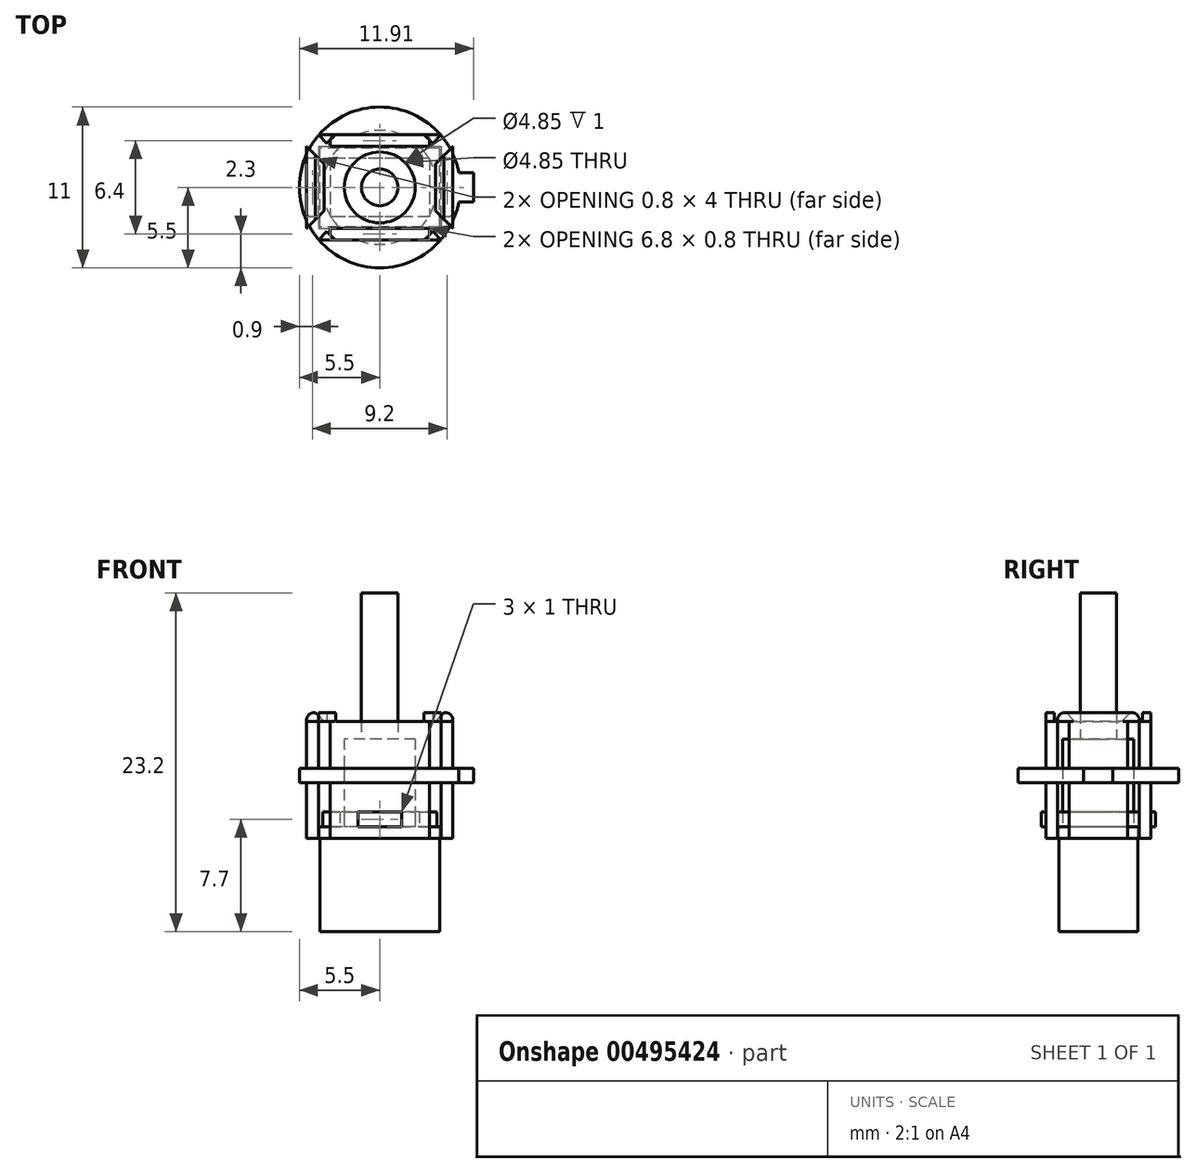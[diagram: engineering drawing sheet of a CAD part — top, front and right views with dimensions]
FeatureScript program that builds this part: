
annotation { "Feature Type Name" : "Feature", "Feature Type Description" : "" }
export const myFeature = defineFeature(function(context is Context, id is Id, definition is map)
    precondition{}
    {
        {
            assignVariable(context, id + "F0", {"name" : "wall", "anyValue" : 0.8});
        }
        {
            assignVariable(context, id + "F1", {"name" : "switch_height", "anyValue" : 7.2});
        }
        {
            var Q0;
            Q0=qCreatedBy(makeId("Top.planeOp"),FACE);
            var sketch = newSketch(context, id + "F2", { "sketchPlane" : qUnion([Q0])});
            skLineSegment(sketch, "E0.bottom", {"start": v(4.1, -2.7) * mm, "end": v(-4.1, -2.7) * mm});
            skLineSegment(sketch, "E0.top", {"start": v(4.1, 2.7) * mm, "end": v(-4.1, 2.7) * mm});
            skLineSegment(sketch, "E0.left", {"start": v(4.1, -2.7) * mm, "end": v(4.1, 2.7) * mm});
            skLineSegment(sketch, "E0.right", {"start": v(-4.1, -2.7) * mm, "end": v(-4.1, 2.7) * mm});
            skPoint(sketch, "E0.middle", {"position": v(0, 0) * mm});
            skCircle(sketch, "E1", {"center": v(0, 0) * mm, "radius": 2.43 * mm});
            skCircle(sketch, "E2", {"center": v(0, 0) * mm, "radius": 3.9 * mm});
            skCircle(sketch, "E3", {"center": v(0, 0) * mm, "radius": 5.5 * mm});
            skLineSegment(sketch, "E4.bottom", {"start": v(5.4, -1) * mm, "end": v(6.4, -1) * mm});
            skLineSegment(sketch, "E4.top", {"start": v(5.4, 1) * mm, "end": v(6.4, 1) * mm});
            skLineSegment(sketch, "E4.left", {"start": v(5.4, -1) * mm, "end": v(5.4, 1) * mm});
            skLineSegment(sketch, "E4.right", {"start": v(6.4, -1) * mm, "end": v(6.4, 1) * mm});
            skPoint(sketch, "E4.middle", {"position": v(5.9, 0) * mm});
            skPoint(sketch, "E4.middle.positionSnap0", {"position": v(4.1, 0) * mm});
            skPoint(sketch, "E4.centerSnap0", {"position": v(4.1, 0) * mm});
            skCircle(sketch, "E5", {"center": v(0, 0) * mm, "radius": 1.25 * mm});
            skSolve(sketch);
        }
        {
            var Q0;
            Q0=makeQuery(id+"F2.imprint","IMPRINT",FACE,{"disambiguationData":[TD([[makeQuery(id+"F2.imprint","IMPRINT",EDGE,{"derivedFrom":sQuery(id+"F2.wireOp",EDGE,"E0.bottom")}),-1.0]])]});
            var Q1;
            Q1=makeQuery(id+"F2.imprint","IMPRINT",FACE,{"disambiguationData":[TD([[makeQuery(id+"F2.imprint","IMPRINT",EDGE,{"derivedFrom":sQuery(id+"F2.wireOp",EDGE,"E1")}),1.0]])]});
            var Q2;
            Q2=makeQuery(id+"F2.imprint","IMPRINT",FACE,{"disambiguationData":[TD([[makeQuery(id+"F2.imprint","IMPRINT",EDGE,{"derivedFrom":sQuery(id+"F2.wireOp",EDGE,"E1")}),-1.0]])]});
            var Q3;
            Q3=makeQuery(id+"F2.imprint","IMPRINT",FACE,{"disambiguationData":[TD([[makeQuery(id+"F2.imprint","IMPRINT",EDGE,{"derivedFrom":sQuery(id+"F2.wireOp",EDGE,"E5")}),1.0]])]});
            extrude(context, id + "F3", {"entities" : qUnion([Q0, Q1, Q2, Q3]), "oppositeDirection" : true, "depth" : (getVariable(context, 'switch_height')) * mm});
        }
        {
            var Q0;
            Q0=makeQuery(id+"F2.imprint","IMPRINT",FACE,{"disambiguationData":[TD([[makeQuery(id+"F2.imprint","IMPRINT",EDGE,{"derivedFrom":sQuery(id+"F2.wireOp",EDGE,"E1")}),1.0]])]});
            var Q1;
            Q1=makeQuery(id+"F2.imprint","IMPRINT",FACE,{"disambiguationData":[TD([[makeQuery(id+"F2.imprint","IMPRINT",EDGE,{"derivedFrom":sQuery(id+"F2.wireOp",EDGE,"E5")}),1.0]])]});
            extrude(context, id + "F4", {"entities" : qUnion([Q0, Q1]), "operationType" : NewBodyOperationType.ADD, "depth" : 6 * mm});
        }
        {
            var Q0;
            Q0=makeQuery(id+"F2.imprint","IMPRINT",FACE,{"disambiguationData":[TD([[makeQuery(id+"F2.imprint","IMPRINT",EDGE,{"derivedFrom":sQuery(id+"F2.wireOp",EDGE,"E1")}),-1.0]])]});
            var Q1;
            {var subQ0=sQuery(id+"F2.wireOp",EDGE,"E2");var subQ1=sQuery(id+"F2.wireOp",EDGE,"E0.bottom");var subQ2=makeQuery(id+"F2.imprint","INTERSECT",VERTEX,{"disambiguationData":[OD(0.0)],"derivedFrom":[subQ1,subQ0]});Q1=makeQuery(id+"F2.imprint","IMPRINT",FACE,{"disambiguationData":[TD([[makeQuery(id+"F2.imprint","IMPRINT",EDGE,{"disambiguationData":[TD([[subQ2,-1.0]])],"derivedFrom":subQ1}),1.0]])]});}
            var Q2;
            {var subQ0=sQuery(id+"F2.wireOp",EDGE,"E2");var subQ1=sQuery(id+"F2.wireOp",EDGE,"E0.top");var subQ2=makeQuery(id+"F2.imprint","INTERSECT",VERTEX,{"disambiguationData":[OD(0.0)],"derivedFrom":[subQ1,subQ0]});Q2=makeQuery(id+"F2.imprint","IMPRINT",FACE,{"disambiguationData":[TD([[makeQuery(id+"F2.imprint","IMPRINT",EDGE,{"disambiguationData":[TD([[subQ2,-1.0]])],"derivedFrom":subQ1}),-1.0]])]});}
            extrude(context, id + "F5", {"entities" : qUnion([Q0, Q1, Q2]), "depth" : 1 * mm});
        }
        {
            var Q0;
            {var subQ0=sQuery(id+"F2.wireOp",EDGE,"E0.left");Q0=makeQuery(id+"F2.imprint","IMPRINT",FACE,{"disambiguationData":[TD([[makeQuery(id+"F2.imprint","IMPRINT",EDGE,{"derivedFrom":subQ0}),-1.0]])]});}
            var Q1;
            {var subQ0=sQuery(id+"F2.wireOp",EDGE,"E0.right");Q1=makeQuery(id+"F2.imprint","IMPRINT",FACE,{"disambiguationData":[TD([[makeQuery(id+"F2.imprint","IMPRINT",EDGE,{"derivedFrom":subQ0}),-1.0]])]});}
            var Q2;
            {var subQ0=sQuery(id+"F2.wireOp",EDGE,"E0.left");Q2=makeQuery(id+"F2.imprint","IMPRINT",FACE,{"disambiguationData":[TD([[makeQuery(id+"F2.imprint","IMPRINT",EDGE,{"derivedFrom":subQ0}),1.0]])]});}
            var Q3;
            {var subQ1=sQuery(id+"F2.wireOp",EDGE,"E4.bottom");Q3=makeQuery(id+"F2.imprint","IMPRINT",FACE,{"disambiguationData":[TD([[makeQuery(id+"F2.imprint","IMPRINT",EDGE,{"derivedFrom":subQ1}),1.0]])]});}
            var Q4;
            {var subQ0=sQuery(id+"F2.wireOp",EDGE,"E4.left");Q4=makeQuery(id+"F2.imprint","IMPRINT",FACE,{"disambiguationData":[TD([[makeQuery(id+"F2.imprint","IMPRINT",EDGE,{"derivedFrom":subQ0}),-1.0]])]});}
            var Q5;
            {var subQ0=sQuery(id+"F2.wireOp",EDGE,"E2");var subQ1=sQuery(id+"F2.wireOp",EDGE,"E0.top");var subQ2=makeQuery(id+"F2.imprint","INTERSECT",VERTEX,{"disambiguationData":[OD(0.0)],"derivedFrom":[subQ1,subQ0]});Q5=makeQuery(id+"F2.imprint","IMPRINT",FACE,{"disambiguationData":[TD([[makeQuery(id+"F2.imprint","IMPRINT",EDGE,{"disambiguationData":[TD([[subQ2,-1.0]])],"derivedFrom":subQ1}),-1.0]])]});}
            var Q6;
            Q6=makeQuery(id+"F2.imprint","IMPRINT",FACE,{"disambiguationData":[TD([[makeQuery(id+"F2.imprint","IMPRINT",EDGE,{"derivedFrom":sQuery(id+"F2.wireOp",EDGE,"E1")}),-1.0]])]});
            var Q7;
            {var subQ0=sQuery(id+"F2.wireOp",EDGE,"E2");var subQ1=sQuery(id+"F2.wireOp",EDGE,"E0.bottom");var subQ2=makeQuery(id+"F2.imprint","INTERSECT",VERTEX,{"disambiguationData":[OD(0.0)],"derivedFrom":[subQ1,subQ0]});Q7=makeQuery(id+"F2.imprint","IMPRINT",FACE,{"disambiguationData":[TD([[makeQuery(id+"F2.imprint","IMPRINT",EDGE,{"disambiguationData":[TD([[subQ2,-1.0]])],"derivedFrom":subQ1}),1.0]])]});}
            extrude(context, id + "F6", {"entities" : qUnion([Q0, Q1, Q2, Q3, Q4, Q5, Q6, Q7]), "depth" : 4 * mm, "hasSecondDirection" : true, "secondDirectionOppositeDirection" : true, "secondDirectionDepth" : -3 * mm});
        }
        {
            var Q0;
            Q0=makeQuery(id+"F2.imprint","IMPRINT",FACE,{"disambiguationData":[TD([[makeQuery(id+"F2.imprint","IMPRINT",EDGE,{"derivedFrom":sQuery(id+"F2.wireOp",EDGE,"E5")}),1.0]])]});
            extrude(context, id + "F7", {"entities" : qUnion([Q0]), "operationType" : NewBodyOperationType.ADD, "depth" : 16 * mm});
        }
        {
            var Q0;
            Q0=qCreatedBy(makeId("Top.planeOp"),FACE);
            var sketch = newSketch(context, id + "F8", { "sketchPlane" : qUnion([Q0])});
            skPoint(sketch, "E6.0", {"position": v(0, 0) * mm});
            skLineSegment(sketch, "E7.0", {"start": v(4.1, -2.7) * mm, "end": v(-4.1, -2.7) * mm, "construction": true});
            skLineSegment(sketch, "E8.0", {"start": v(-4.1, -2.7) * mm, "end": v(-4.1, 2.7) * mm, "construction": true});
            skLineSegment(sketch, "E9.0", {"start": v(4.1, 2.7) * mm, "end": v(-4.1, 2.7) * mm, "construction": true});
            skLineSegment(sketch, "E10.0", {"start": v(4.1, -2.7) * mm, "end": v(4.1, 2.7) * mm, "construction": true});
            skLineSegment(sketch, "E11.bottom", {"start": v(5, 2) * mm, "end": v(-5, 2) * mm});
            skLineSegment(sketch, "E11.top", {"start": v(5, -2) * mm, "end": v(-5, -2) * mm});
            skLineSegment(sketch, "E11.left", {"start": v(5, 2) * mm, "end": v(5, -2) * mm});
            skLineSegment(sketch, "E11.right", {"start": v(-5, 2) * mm, "end": v(-5, -2) * mm});
            skLineSegment(sketch, "E12.bottom", {"start": v(3.4, 3.6) * mm, "end": v(-3.4, 3.6) * mm});
            skLineSegment(sketch, "E12.top", {"start": v(3.4, -3.6) * mm, "end": v(-3.4, -3.6) * mm});
            skLineSegment(sketch, "E12.left", {"start": v(3.4, 3.6) * mm, "end": v(3.4, -3.6) * mm});
            skLineSegment(sketch, "E12.right", {"start": v(-3.4, 3.6) * mm, "end": v(-3.4, -3.6) * mm});
            skLineSegment(sketch, "E13.bottom", {"start": v(-4.2, 2.8) * mm, "end": v(4.2, 2.8) * mm});
            skLineSegment(sketch, "E13.top", {"start": v(-4.2, -2.8) * mm, "end": v(4.2, -2.8) * mm});
            skLineSegment(sketch, "E13.left", {"start": v(-4.2, 2.8) * mm, "end": v(-4.2, -2.8) * mm});
            skLineSegment(sketch, "E13.right", {"start": v(4.2, 2.8) * mm, "end": v(4.2, -2.8) * mm});
            skSolve(sketch);
        }
        {
            var Q0;
            {var subQ0=sQuery(id+"F8.wireOp",EDGE,"E12.left");var subQ1=sQuery(id+"F8.wireOp",EDGE,"E9.0");var subQ2=makeQuery(id+"F8.imprint","INTERSECT",VERTEX,{"derivedFrom":[subQ1,subQ0]});Q0=makeQuery(id+"F8.imprint","IMPRINT",FACE,{"disambiguationData":[TD([[makeQuery(id+"F8.imprint","IMPRINT",EDGE,{"disambiguationData":[TD([[subQ2,-1.0]])],"derivedFrom":subQ1}),1.0]])]});}
            var Q1;
            {var subQ0=sQuery(id+"F8.wireOp",EDGE,"E9.0");var subQ1=sQuery(id+"F8.wireOp",EDGE,"E8.0");var subQ2=makeQuery(id+"F8.imprint","INTERSECT",VERTEX,{"derivedFrom":[subQ1,subQ0]});Q1=makeQuery(id+"F8.imprint","IMPRINT",FACE,{"disambiguationData":[TD([[makeQuery(id+"F8.imprint","IMPRINT",EDGE,{"disambiguationData":[TD([[subQ2,1.0]])],"derivedFrom":subQ1}),-1.0]])]});}
            var Q2;
            {var subQ0=sQuery(id+"F8.wireOp",EDGE,"E11.top");var subQ1=sQuery(id+"F8.wireOp",EDGE,"E8.0");var subQ2=makeQuery(id+"F8.imprint","INTERSECT",VERTEX,{"derivedFrom":[subQ1,subQ0]});Q2=makeQuery(id+"F8.imprint","IMPRINT",FACE,{"disambiguationData":[TD([[makeQuery(id+"F8.imprint","IMPRINT",EDGE,{"disambiguationData":[TD([[subQ2,-1.0]])],"derivedFrom":subQ1}),-1.0]])]});}
            var Q3;
            {var subQ0=sQuery(id+"F8.wireOp",EDGE,"E8.0");var subQ1=sQuery(id+"F8.wireOp",EDGE,"E7.0");var subQ2=makeQuery(id+"F8.imprint","INTERSECT",VERTEX,{"derivedFrom":[subQ1,subQ0]});Q3=makeQuery(id+"F8.imprint","IMPRINT",FACE,{"disambiguationData":[TD([[makeQuery(id+"F8.imprint","IMPRINT",EDGE,{"disambiguationData":[TD([[subQ2,1.0]])],"derivedFrom":subQ1}),-1.0]])]});}
            var Q4;
            {var subQ0=sQuery(id+"F8.wireOp",EDGE,"E12.left");var subQ1=sQuery(id+"F8.wireOp",EDGE,"E7.0");var subQ2=makeQuery(id+"F8.imprint","INTERSECT",VERTEX,{"derivedFrom":[subQ1,subQ0]});Q4=makeQuery(id+"F8.imprint","IMPRINT",FACE,{"disambiguationData":[TD([[makeQuery(id+"F8.imprint","IMPRINT",EDGE,{"disambiguationData":[TD([[subQ2,-1.0]])],"derivedFrom":subQ1}),-1.0]])]});}
            var Q5;
            {var subQ0=sQuery(id+"F8.wireOp",EDGE,"E11.top");var subQ1=sQuery(id+"F8.wireOp",EDGE,"E10.0");var subQ2=makeQuery(id+"F8.imprint","INTERSECT",VERTEX,{"derivedFrom":[subQ1,subQ0]});Q5=makeQuery(id+"F8.imprint","IMPRINT",FACE,{"disambiguationData":[TD([[makeQuery(id+"F8.imprint","IMPRINT",EDGE,{"disambiguationData":[TD([[subQ2,-1.0]])],"derivedFrom":subQ1}),1.0]])]});}
            var Q6;
            {var subQ0=sQuery(id+"F8.wireOp",EDGE,"E10.0");var subQ1=sQuery(id+"F8.wireOp",EDGE,"E7.0");var subQ2=makeQuery(id+"F8.imprint","INTERSECT",VERTEX,{"derivedFrom":[subQ1,subQ0]});Q6=makeQuery(id+"F8.imprint","IMPRINT",FACE,{"disambiguationData":[TD([[makeQuery(id+"F8.imprint","IMPRINT",EDGE,{"disambiguationData":[TD([[subQ2,-1.0]])],"derivedFrom":subQ1}),-1.0]])]});}
            var Q7;
            {var subQ0=sQuery(id+"F8.wireOp",EDGE,"E10.0");var subQ1=sQuery(id+"F8.wireOp",EDGE,"E9.0");var subQ2=makeQuery(id+"F8.imprint","INTERSECT",VERTEX,{"derivedFrom":[subQ1,subQ0]});Q7=makeQuery(id+"F8.imprint","IMPRINT",FACE,{"disambiguationData":[TD([[makeQuery(id+"F8.imprint","IMPRINT",EDGE,{"disambiguationData":[TD([[subQ2,-1.0]])],"derivedFrom":subQ1}),1.0]])]});}
            var Q8;
            {var subQ0=sQuery(id+"F8.wireOp",EDGE,"E11.right");Q8=makeQuery(id+"F8.imprint","IMPRINT",FACE,{"disambiguationData":[TD([[makeQuery(id+"F8.imprint","IMPRINT",EDGE,{"derivedFrom":subQ0}),1.0]])]});}
            var Q9;
            {var subQ0=sQuery(id+"F8.wireOp",EDGE,"E13.left");var subQ1=sQuery(id+"F8.wireOp",EDGE,"E11.bottom");var subQ2=makeQuery(id+"F8.imprint","INTERSECT",VERTEX,{"derivedFrom":[subQ1,subQ0]});Q9=makeQuery(id+"F8.imprint","IMPRINT",FACE,{"disambiguationData":[TD([[makeQuery(id+"F8.imprint","IMPRINT",EDGE,{"disambiguationData":[TD([[subQ2,1.0]])],"derivedFrom":subQ1}),1.0]])]});}
            var Q10;
            {var subQ0=sQuery(id+"F8.wireOp",EDGE,"E12.left");var subQ1=sQuery(id+"F8.wireOp",EDGE,"E11.bottom");var subQ2=makeQuery(id+"F8.imprint","INTERSECT",VERTEX,{"derivedFrom":[subQ1,subQ0]});Q10=makeQuery(id+"F8.imprint","IMPRINT",FACE,{"disambiguationData":[TD([[makeQuery(id+"F8.imprint","IMPRINT",EDGE,{"disambiguationData":[TD([[subQ2,-1.0]])],"derivedFrom":subQ1}),-1.0]])]});}
            var Q11;
            {var subQ0=sQuery(id+"F8.wireOp",EDGE,"E13.left");var subQ1=sQuery(id+"F8.wireOp",EDGE,"E11.bottom");var subQ2=makeQuery(id+"F8.imprint","INTERSECT",VERTEX,{"derivedFrom":[subQ1,subQ0]});Q11=makeQuery(id+"F8.imprint","IMPRINT",FACE,{"disambiguationData":[TD([[makeQuery(id+"F8.imprint","IMPRINT",EDGE,{"disambiguationData":[TD([[subQ2,1.0]])],"derivedFrom":subQ1}),-1.0]])]});}
            var Q12;
            {var subQ0=sQuery(id+"F8.wireOp",EDGE,"E12.bottom");Q12=makeQuery(id+"F8.imprint","IMPRINT",FACE,{"disambiguationData":[TD([[makeQuery(id+"F8.imprint","IMPRINT",EDGE,{"derivedFrom":subQ0}),1.0]])]});}
            var Q13;
            {var subQ0=sQuery(id+"F8.wireOp",EDGE,"E13.left");var subQ1=sQuery(id+"F8.wireOp",EDGE,"E11.top");var subQ2=makeQuery(id+"F8.imprint","INTERSECT",VERTEX,{"derivedFrom":[subQ1,subQ0]});Q13=makeQuery(id+"F8.imprint","IMPRINT",FACE,{"disambiguationData":[TD([[makeQuery(id+"F8.imprint","IMPRINT",EDGE,{"disambiguationData":[TD([[subQ2,1.0]])],"derivedFrom":subQ1}),1.0]])]});}
            var Q14;
            {var subQ0=sQuery(id+"F8.wireOp",EDGE,"E12.left");var subQ1=sQuery(id+"F8.wireOp",EDGE,"E11.top");var subQ2=makeQuery(id+"F8.imprint","INTERSECT",VERTEX,{"derivedFrom":[subQ1,subQ0]});Q14=makeQuery(id+"F8.imprint","IMPRINT",FACE,{"disambiguationData":[TD([[makeQuery(id+"F8.imprint","IMPRINT",EDGE,{"disambiguationData":[TD([[subQ2,-1.0]])],"derivedFrom":subQ1}),1.0]])]});}
            var Q15;
            {var subQ0=sQuery(id+"F8.wireOp",EDGE,"E12.top");Q15=makeQuery(id+"F8.imprint","IMPRINT",FACE,{"disambiguationData":[TD([[makeQuery(id+"F8.imprint","IMPRINT",EDGE,{"derivedFrom":subQ0}),-1.0]])]});}
            var Q16;
            {var subQ0=sQuery(id+"F8.wireOp",EDGE,"E11.left");Q16=makeQuery(id+"F8.imprint","IMPRINT",FACE,{"disambiguationData":[TD([[makeQuery(id+"F8.imprint","IMPRINT",EDGE,{"derivedFrom":subQ0}),-1.0]])]});}
            var Q17;
            {var subQ0=sQuery(id+"F8.wireOp",EDGE,"E13.right");var subQ1=sQuery(id+"F8.wireOp",EDGE,"E11.bottom");var subQ2=makeQuery(id+"F8.imprint","INTERSECT",VERTEX,{"derivedFrom":[subQ1,subQ0]});Q17=makeQuery(id+"F8.imprint","IMPRINT",FACE,{"disambiguationData":[TD([[makeQuery(id+"F8.imprint","IMPRINT",EDGE,{"disambiguationData":[TD([[subQ2,-1.0]])],"derivedFrom":subQ1}),1.0]])]});}
            var Q18;
            {var subQ0=sQuery(id+"F8.wireOp",EDGE,"E13.right");var subQ1=sQuery(id+"F8.wireOp",EDGE,"E11.top");var subQ2=makeQuery(id+"F8.imprint","INTERSECT",VERTEX,{"derivedFrom":[subQ1,subQ0]});Q18=makeQuery(id+"F8.imprint","IMPRINT",FACE,{"disambiguationData":[TD([[makeQuery(id+"F8.imprint","IMPRINT",EDGE,{"disambiguationData":[TD([[subQ2,-1.0]])],"derivedFrom":subQ1}),1.0]])]});}
            var Q19;
            {var subQ0=sQuery(id+"F8.wireOp",EDGE,"E13.right");var subQ1=sQuery(id+"F8.wireOp",EDGE,"E11.bottom");var subQ2=makeQuery(id+"F8.imprint","INTERSECT",VERTEX,{"derivedFrom":[subQ1,subQ0]});Q19=makeQuery(id+"F8.imprint","IMPRINT",FACE,{"disambiguationData":[TD([[makeQuery(id+"F8.imprint","IMPRINT",EDGE,{"disambiguationData":[TD([[subQ2,-1.0]])],"derivedFrom":subQ1}),-1.0]])]});}
            extrude(context, id + "F9", {"entities" : qUnion([Q0, Q1, Q2, Q3, Q4, Q5, Q6, Q7, Q8, Q9, Q10, Q11, Q12, Q13, Q14, Q15, Q16, Q17, Q18, Q19]), "oppositeDirection" : true, "depth" : (getVariable(context, 'wall')) * mm});
        }
        {
            var Q0;
            {var subQ5=sQuery(id+"F8.wireOp",EDGE,"E11.right");Q0=makeQuery(id+"F8.imprint","IMPRINT",FACE,{"disambiguationData":[TD([[makeQuery(id+"F8.imprint","IMPRINT",EDGE,{"derivedFrom":subQ5}),1.0]])]});}
            var Q1;
            {var subQ5=sQuery(id+"F8.wireOp",EDGE,"E11.left");Q1=makeQuery(id+"F8.imprint","IMPRINT",FACE,{"disambiguationData":[TD([[makeQuery(id+"F8.imprint","IMPRINT",EDGE,{"derivedFrom":subQ5}),-1.0]])]});}
            var Q2;
            {var subQ5=sQuery(id+"F8.wireOp",EDGE,"E12.top");Q2=makeQuery(id+"F8.imprint","IMPRINT",FACE,{"disambiguationData":[TD([[makeQuery(id+"F8.imprint","IMPRINT",EDGE,{"derivedFrom":subQ5}),-1.0]])]});}
            var Q3;
            {var subQ5=sQuery(id+"F8.wireOp",EDGE,"E12.bottom");Q3=makeQuery(id+"F8.imprint","IMPRINT",FACE,{"disambiguationData":[TD([[makeQuery(id+"F8.imprint","IMPRINT",EDGE,{"derivedFrom":subQ5}),1.0]])]});}
            extrude(context, id + "F10", {"entities" : qUnion([Q0, Q1, Q2, Q3]), "operationType" : NewBodyOperationType.ADD, "depth" : (getVariable(context, 'switch_height')) * mm, "hasSecondDirection" : true, "secondDirectionOppositeDirection" : true, "secondDirectionDepth" : (getVariable(context, 'wall')) * mm});
        }
        {
            var Q0;
            Q0=makeQuery(id+"F10.opExtrude","CAP_FACE",FACE,{"disambiguationData":[OSD([sQuery(id+"F8.wireOp",EDGE,"E11.bottom"),sQuery(id+"F8.wireOp",EDGE,"E11.top"),sQuery(id+"F8.wireOp",EDGE,"E11.left"),sQuery(id+"F8.wireOp",EDGE,"E13.right")])],"isStart":false});
            var sketch = newSketch(context, id + "F11", { "sketchPlane" : qUnion([Q0])});
            skLineSegment(sketch, "E14.0", {"start": v(-4.2, 2.8) * mm, "end": v(4.2, 2.8) * mm, "construction": true});
            skLineSegment(sketch, "E15.0", {"start": v(4.2, 2.8) * mm, "end": v(4.2, -2.8) * mm, "construction": true});
            skLineSegment(sketch, "E16.0", {"start": v(-4.2, -2.8) * mm, "end": v(4.2, -2.8) * mm, "construction": true});
            skLineSegment(sketch, "E17.0", {"start": v(-4.2, 2.8) * mm, "end": v(-4.2, -2.8) * mm, "construction": true});
            skCircle(sketch, "E18.0", {"center": v(0, 0) * mm, "radius": 3.9 * mm, "construction": true});
            skLineSegment(sketch, "E19.bottom", {"start": v(-5, 3.6) * mm, "end": v(5, 3.6) * mm});
            skLineSegment(sketch, "E19.top", {"start": v(-5, -3.6) * mm, "end": v(5, -3.6) * mm});
            skLineSegment(sketch, "E19.left", {"start": v(-5, 3.6) * mm, "end": v(-5, -3.6) * mm});
            skLineSegment(sketch, "E19.right", {"start": v(5, 3.6) * mm, "end": v(5, -3.6) * mm});
            skLineSegment(sketch, "E20.bottom", {"start": v(-3.4, 2) * mm, "end": v(3.4, 2) * mm});
            skLineSegment(sketch, "E20.top", {"start": v(-3.4, -2) * mm, "end": v(3.4, -2) * mm});
            skLineSegment(sketch, "E20.left", {"start": v(-3.4, 2) * mm, "end": v(-3.4, -2) * mm});
            skLineSegment(sketch, "E20.right", {"start": v(3.4, 2) * mm, "end": v(3.4, -2) * mm});
            skLineSegment(sketch, "E21", {"start": v(-5, 3.6) * mm, "end": v(-3.4, 2) * mm, "construction": true});
            skCircle(sketch, "E22", {"center": v(0, 0) * mm, "radius": 4.7 * mm});
            skLineSegment(sketch, "E23", {"start": v(-5, 2.8) * mm, "end": v(-3.4, 1.2) * mm});
            skLineSegment(sketch, "E24", {"start": v(-4.2, 3.6) * mm, "end": v(-2.6, 2) * mm});
            skLineSegment(sketch, "E25", {"start": v(-0.75, 0.75) * mm, "end": v(0.75, -0.75) * mm, "construction": true});
            skLineSegment(sketch, "E26", {"start": v(0.75, 0.75) * mm, "end": v(-0.75, -0.75) * mm, "construction": true});
            skLineSegment(sketch, "E27", {"start": v(3.4, -1.2) * mm, "end": v(5, -2.8) * mm});
            skLineSegment(sketch, "E28", {"start": v(2.6, -2) * mm, "end": v(4.2, -3.6) * mm});
            skLineSegment(sketch, "E29", {"start": v(-3.4, -1.2) * mm, "end": v(-5, -2.8) * mm});
            skLineSegment(sketch, "E30", {"start": v(-2.6, -2) * mm, "end": v(-4.2, -3.6) * mm});
            skLineSegment(sketch, "E31", {"start": v(4.2, 3.6) * mm, "end": v(2.6, 2) * mm});
            skLineSegment(sketch, "E32", {"start": v(3.4, 1.2) * mm, "end": v(5, 2.8) * mm});
            skSolve(sketch);
        }
        {
            var Q0;
            {var subQ0=sQuery(id+"F11.wireOp",EDGE,"E23");var subQ1=sQuery(id+"F11.wireOp",EDGE,"E19.left");var subQ2=makeQuery(id+"F11.imprint","INTERSECT",VERTEX,{"derivedFrom":[subQ1,subQ0]});Q0=makeQuery(id+"F11.imprint","IMPRINT",FACE,{"disambiguationData":[TD([[makeQuery(id+"F11.imprint","IMPRINT",EDGE,{"disambiguationData":[TD([[subQ2,-1.0]])],"derivedFrom":subQ1}),1.0]])]});}
            var Q1;
            {var subQ0=sQuery(id+"F11.wireOp",EDGE,"E32");var subQ1=sQuery(id+"F11.wireOp",EDGE,"E22");var subQ2=makeQuery(id+"F11.imprint","INTERSECT",VERTEX,{"derivedFrom":[subQ1,subQ0]});Q1=makeQuery(id+"F11.imprint","IMPRINT",FACE,{"disambiguationData":[TD([[makeQuery(id+"F11.imprint","IMPRINT",EDGE,{"disambiguationData":[TD([[subQ2,1.0]])],"derivedFrom":subQ1}),-1.0]])]});}
            var Q2;
            {var subQ0=sQuery(id+"F11.wireOp",EDGE,"E27");var subQ1=sQuery(id+"F11.wireOp",EDGE,"E22");var subQ2=makeQuery(id+"F11.imprint","INTERSECT",VERTEX,{"derivedFrom":[subQ1,subQ0]});Q2=makeQuery(id+"F11.imprint","IMPRINT",FACE,{"disambiguationData":[TD([[makeQuery(id+"F11.imprint","IMPRINT",EDGE,{"disambiguationData":[TD([[subQ2,-1.0]])],"derivedFrom":subQ1}),-1.0]])]});}
            var Q3;
            {var subQ0=sQuery(id+"F8.wireOp",EDGE,"E11.left");var subQ1=sQuery(id+"F8.wireOp",EDGE,"E11.bottom");var subQ3=makeQuery(id+"F10.opExtrude","CAP_EDGE",EDGE,{"disambiguationData":[OSD([subQ1]),TDD([makeQuery(id+"F8.imprint","IMPRINT",EDGE,{"disambiguationData":[TD([[makeQuery(id+"F8.imprint","INTERSECT",VERTEX,{"derivedFrom":[subQ1,subQ0]}),-1.0]])],"derivedFrom":subQ1})])],"isStart":false});Q3=makeQuery(id+"F11.imprint","IMPRINT",FACE,{"disambiguationData":[TD([[makeQuery(id+"F11.imprint","IMPRINT",EDGE,{"derivedFrom":subQ3}),1.0]])]});}
            var Q4;
            {var subQ0=sQuery(id+"F11.wireOp",EDGE,"E24");var subQ1=sQuery(id+"F11.wireOp",EDGE,"E19.bottom");var subQ2=makeQuery(id+"F11.imprint","INTERSECT",VERTEX,{"derivedFrom":[subQ1,subQ0]});Q4=makeQuery(id+"F11.imprint","IMPRINT",FACE,{"disambiguationData":[TD([[makeQuery(id+"F11.imprint","IMPRINT",EDGE,{"disambiguationData":[TD([[subQ2,-1.0]])],"derivedFrom":subQ1}),-1.0]])]});}
            var Q5;
            {var subQ0=sQuery(id+"F8.wireOp",EDGE,"E11.left");var subQ1=sQuery(id+"F8.wireOp",EDGE,"E11.bottom");var subQ3=makeQuery(id+"F10.opExtrude","CAP_EDGE",EDGE,{"disambiguationData":[OSD([subQ1]),TDD([makeQuery(id+"F8.imprint","IMPRINT",EDGE,{"disambiguationData":[TD([[makeQuery(id+"F8.imprint","INTERSECT",VERTEX,{"derivedFrom":[subQ1,subQ0]}),-1.0]])],"derivedFrom":subQ1})])],"isStart":false});Q5=makeQuery(id+"F11.imprint","IMPRINT",FACE,{"disambiguationData":[TD([[makeQuery(id+"F11.imprint","IMPRINT",EDGE,{"derivedFrom":subQ3}),1.0]])]});}
            var Q6;
            {var subQ0=sQuery(id+"F11.wireOp",EDGE,"E28");var subQ1=sQuery(id+"F11.wireOp",EDGE,"E19.top");var subQ2=makeQuery(id+"F11.imprint","INTERSECT",VERTEX,{"derivedFrom":[subQ1,subQ0]});Q6=makeQuery(id+"F11.imprint","IMPRINT",FACE,{"disambiguationData":[TD([[makeQuery(id+"F11.imprint","IMPRINT",EDGE,{"disambiguationData":[TD([[subQ2,1.0]])],"derivedFrom":subQ1}),1.0]])]});}
            var Q7;
            {var subQ0=sQuery(id+"F11.wireOp",EDGE,"E31");var subQ1=sQuery(id+"F11.wireOp",EDGE,"E19.bottom");var subQ2=makeQuery(id+"F11.imprint","INTERSECT",VERTEX,{"derivedFrom":[subQ1,subQ0]});Q7=makeQuery(id+"F11.imprint","IMPRINT",FACE,{"disambiguationData":[TD([[makeQuery(id+"F11.imprint","IMPRINT",EDGE,{"disambiguationData":[TD([[subQ2,1.0]])],"derivedFrom":subQ1}),-1.0]])]});}
            var Q8;
            {var subQ0=sQuery(id+"F11.wireOp",EDGE,"E30");var subQ1=sQuery(id+"F11.wireOp",EDGE,"E19.top");var subQ2=makeQuery(id+"F11.imprint","INTERSECT",VERTEX,{"derivedFrom":[subQ1,subQ0]});Q8=makeQuery(id+"F11.imprint","IMPRINT",FACE,{"disambiguationData":[TD([[makeQuery(id+"F11.imprint","IMPRINT",EDGE,{"disambiguationData":[TD([[subQ2,-1.0]])],"derivedFrom":subQ1}),1.0]])]});}
            var Q9;
            {var subQ1=sQuery(id+"F8.wireOp",EDGE,"E11.top");var subQ3=makeQuery(id+"F10.opExtrude","CAP_EDGE",EDGE,{"disambiguationData":[OSD([subQ1]),TDD([makeQuery(id+"F8.imprint","IMPRINT",EDGE,{"disambiguationData":[TD([[makeQuery(id+"F8.imprint","INTERSECT",VERTEX,{"derivedFrom":[subQ1,sQuery(id+"F8.wireOp",EDGE,"E11.left")]}),-1.0]])],"derivedFrom":subQ1})])],"isStart":false});Q9=makeQuery(id+"F11.imprint","IMPRINT",FACE,{"disambiguationData":[TD([[makeQuery(id+"F11.imprint","IMPRINT",EDGE,{"derivedFrom":subQ3}),1.0]])]});}
            var Q10;
            {var subQ1=sQuery(id+"F8.wireOp",EDGE,"E11.bottom");var subQ3=makeQuery(id+"F10.opExtrude","CAP_EDGE",EDGE,{"disambiguationData":[OSD([subQ1]),TDD([makeQuery(id+"F8.imprint","IMPRINT",EDGE,{"disambiguationData":[TD([[makeQuery(id+"F8.imprint","INTERSECT",VERTEX,{"derivedFrom":[subQ1,sQuery(id+"F8.wireOp",EDGE,"E11.left")]}),-1.0]])],"derivedFrom":subQ1})])],"isStart":false});Q10=makeQuery(id+"F11.imprint","IMPRINT",FACE,{"disambiguationData":[TD([[makeQuery(id+"F11.imprint","IMPRINT",EDGE,{"derivedFrom":subQ3}),-1.0]])]});}
            var Q11;
            {var subQ0=sQuery(id+"F11.wireOp",EDGE,"E23");var subQ1=sQuery(id+"F11.wireOp",EDGE,"E20.left");var subQ2=makeQuery(id+"F11.imprint","INTERSECT",VERTEX,{"derivedFrom":[subQ1,subQ0]});Q11=makeQuery(id+"F11.imprint","IMPRINT",FACE,{"disambiguationData":[TD([[makeQuery(id+"F11.imprint","IMPRINT",EDGE,{"disambiguationData":[TD([[subQ2,-1.0]])],"derivedFrom":subQ1}),-1.0]])]});}
            var Q12;
            {var subQ0=sQuery(id+"F11.wireOp",EDGE,"E27");var subQ1=sQuery(id+"F11.wireOp",EDGE,"E20.right");var subQ2=makeQuery(id+"F11.imprint","INTERSECT",VERTEX,{"derivedFrom":[subQ1,subQ0]});Q12=makeQuery(id+"F11.imprint","IMPRINT",FACE,{"disambiguationData":[TD([[makeQuery(id+"F11.imprint","IMPRINT",EDGE,{"disambiguationData":[TD([[subQ2,1.0]])],"derivedFrom":subQ1}),1.0]])]});}
            var Q13;
            {var subQ0=sQuery(id+"F11.wireOp",EDGE,"E22");var subQ1=makeQuery(id+"F10.opExtrude","CAP_EDGE",EDGE,{"disambiguationData":[OSD([sQuery(id+"F8.wireOp",EDGE,"E13.right")])],"isStart":false});var subQ2=makeQuery(id+"F11.imprint","INTERSECT",VERTEX,{"disambiguationData":[OD(0.0)],"derivedFrom":[subQ1,subQ0]});Q13=makeQuery(id+"F11.imprint","IMPRINT",FACE,{"disambiguationData":[TD([[makeQuery(id+"F11.imprint","IMPRINT",EDGE,{"disambiguationData":[TD([[subQ2,1.0]])],"derivedFrom":subQ0}),1.0]])]});}
            extrude(context, id + "F12", {"entities" : qUnion([Q0, Q1, Q2, Q3, Q4, Q5, Q6, Q7, Q8, Q9, Q10, Q11, Q12, Q13]), "operationType" : NewBodyOperationType.ADD, "depth" : 0.6 * mm, "offsetDistance" : 25 * mm});
        }
        {
            var Q0;
            Q0=makeQuery(id+"F12.opExtrude","CAP_EDGE",EDGE,{"disambiguationData":[OSD([sQuery(id+"F11.wireOp",EDGE,"E19.left")])],"isStart":false});
            var Q1;
            Q1=makeQuery(id+"F12.opExtrude","CAP_EDGE",EDGE,{"disambiguationData":[OSD([sQuery(id+"F11.wireOp",EDGE,"E19.right")])],"isStart":false});
            fillet(context, id + "F13", {"entities" : qUnion([Q0, Q1]), "radius" : 0.5 * mm, "allowEdgeOverflow" : false});
        }
        {
            var Q0;
            {var subQ0=sQuery(id+"F8.wireOp",EDGE,"E11.left");var subQ1=sQuery(id+"F8.wireOp",EDGE,"E11.bottom");Q0=makeQuery(id+"F10.boolean.opBoolean","MERGE",EDGE,{"derivedFrom":[makeQuery(id+"F9.opExtrude","SWEPT_EDGE",EDGE,{"disambiguationData":[OSD([subQ1,subQ0])]}),makeQuery(id+"F10.opExtrude","SWEPT_EDGE",EDGE,{"disambiguationData":[OSD([subQ1,subQ0])]})]});}
            var Q1;
            {var subQ0=sQuery(id+"F8.wireOp",EDGE,"E12.left");var subQ1=sQuery(id+"F8.wireOp",EDGE,"E12.bottom");Q1=makeQuery(id+"F10.boolean.opBoolean","MERGE",EDGE,{"derivedFrom":[makeQuery(id+"F9.opExtrude","SWEPT_EDGE",EDGE,{"disambiguationData":[OSD([subQ1,subQ0])]}),makeQuery(id+"F10.opExtrude","SWEPT_EDGE",EDGE,{"disambiguationData":[OSD([subQ1,subQ0])]})]});}
            var Q2;
            {var subQ0=sQuery(id+"F8.wireOp",EDGE,"E12.right");var subQ1=sQuery(id+"F8.wireOp",EDGE,"E12.bottom");Q2=makeQuery(id+"F10.boolean.opBoolean","MERGE",EDGE,{"derivedFrom":[makeQuery(id+"F9.opExtrude","SWEPT_EDGE",EDGE,{"disambiguationData":[OSD([subQ1,subQ0])]}),makeQuery(id+"F10.opExtrude","SWEPT_EDGE",EDGE,{"disambiguationData":[OSD([subQ1,subQ0])]})]});}
            var Q3;
            {var subQ0=sQuery(id+"F8.wireOp",EDGE,"E11.left");var subQ1=sQuery(id+"F8.wireOp",EDGE,"E11.top");Q3=makeQuery(id+"F10.boolean.opBoolean","MERGE",EDGE,{"derivedFrom":[makeQuery(id+"F9.opExtrude","SWEPT_EDGE",EDGE,{"disambiguationData":[OSD([subQ1,subQ0])]}),makeQuery(id+"F10.opExtrude","SWEPT_EDGE",EDGE,{"disambiguationData":[OSD([subQ1,subQ0])]})]});}
            var Q4;
            {var subQ0=sQuery(id+"F8.wireOp",EDGE,"E12.left");var subQ1=sQuery(id+"F8.wireOp",EDGE,"E12.top");Q4=makeQuery(id+"F10.boolean.opBoolean","MERGE",EDGE,{"derivedFrom":[makeQuery(id+"F9.opExtrude","SWEPT_EDGE",EDGE,{"disambiguationData":[OSD([subQ1,subQ0])]}),makeQuery(id+"F10.opExtrude","SWEPT_EDGE",EDGE,{"disambiguationData":[OSD([subQ1,subQ0])]})]});}
            var Q5;
            {var subQ0=sQuery(id+"F8.wireOp",EDGE,"E12.right");var subQ1=sQuery(id+"F8.wireOp",EDGE,"E12.top");Q5=makeQuery(id+"F10.boolean.opBoolean","MERGE",EDGE,{"derivedFrom":[makeQuery(id+"F9.opExtrude","SWEPT_EDGE",EDGE,{"disambiguationData":[OSD([subQ1,subQ0])]}),makeQuery(id+"F10.opExtrude","SWEPT_EDGE",EDGE,{"disambiguationData":[OSD([subQ1,subQ0])]})]});}
            var Q6;
            {var subQ0=sQuery(id+"F8.wireOp",EDGE,"E11.right");var subQ1=sQuery(id+"F8.wireOp",EDGE,"E11.top");Q6=makeQuery(id+"F10.boolean.opBoolean","MERGE",EDGE,{"derivedFrom":[makeQuery(id+"F9.opExtrude","SWEPT_EDGE",EDGE,{"disambiguationData":[OSD([subQ1,subQ0])]}),makeQuery(id+"F10.opExtrude","SWEPT_EDGE",EDGE,{"disambiguationData":[OSD([subQ1,subQ0])]})]});}
            fillet(context, id + "F14", {"entities" : qUnion([Q0, Q1, Q2, Q3, Q4, Q5, Q6]), "radius" : 0.3 * mm, "tangentPropagation" : true, "allowEdgeOverflow" : false});
        }
        {
            var Q0;
            Q0=makeQuery(id+"F12.opExtrude","CAP_EDGE",EDGE,{"disambiguationData":[OSD([sQuery(id+"F11.wireOp",EDGE,"E20.right")])],"isStart":false});
            var Q1;
            Q1=makeQuery(id+"F12.opExtrude","CAP_EDGE",EDGE,{"disambiguationData":[OSD([sQuery(id+"F11.wireOp",EDGE,"E20.left")])],"isStart":false});
            chamfer(context, id + "F15", {"entities" : qUnion([Q0, Q1]), "width" : 1 * mm, "tangentPropagation" : true});
        }
    });
